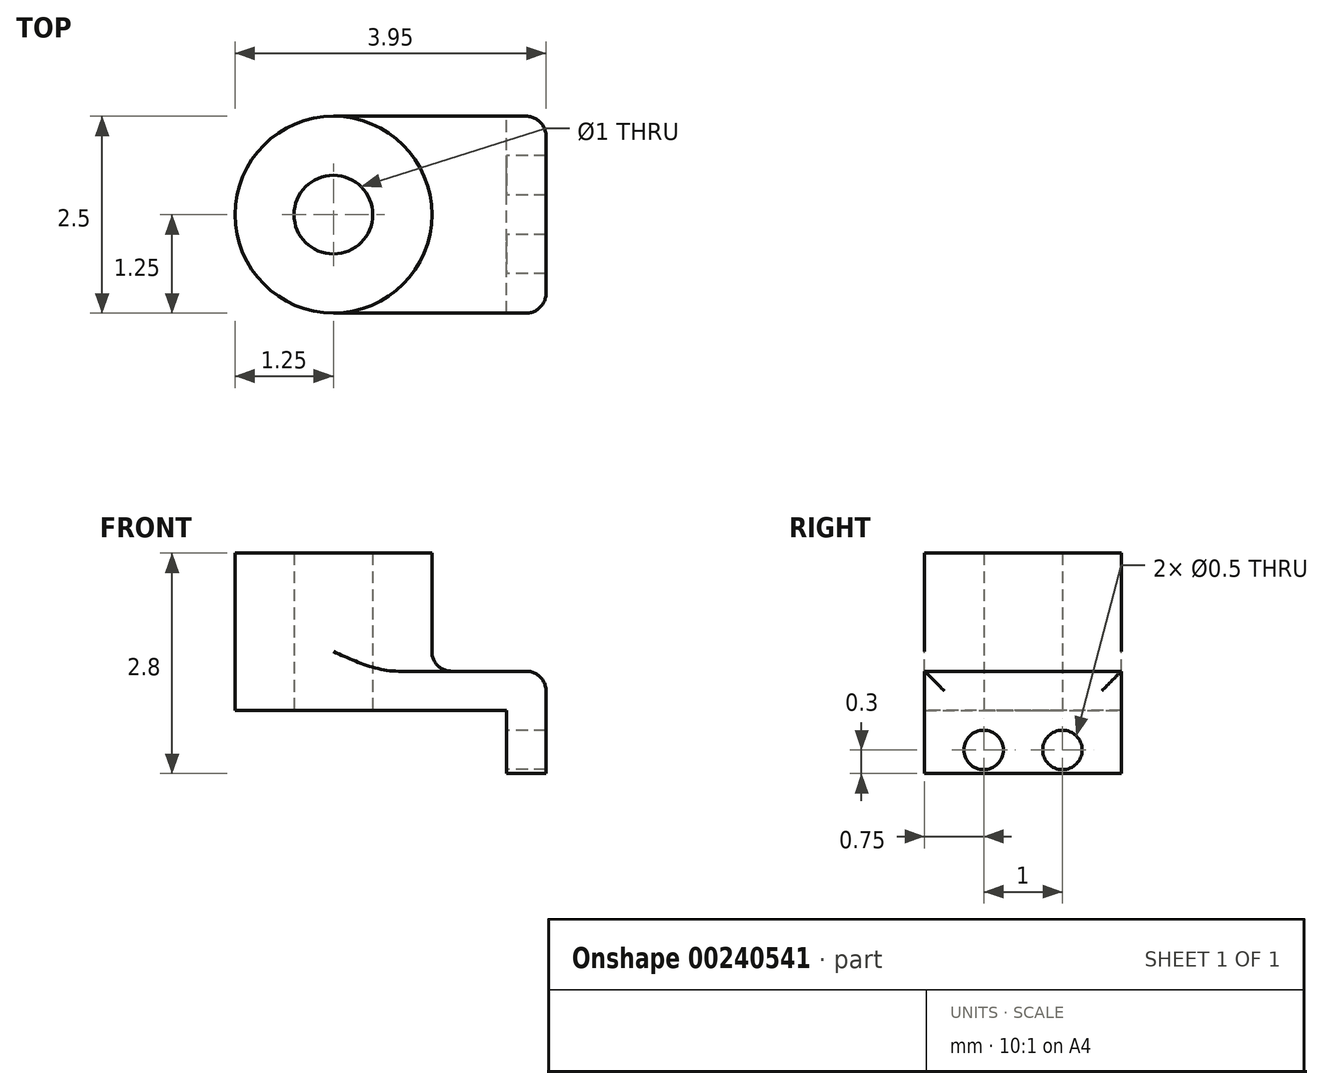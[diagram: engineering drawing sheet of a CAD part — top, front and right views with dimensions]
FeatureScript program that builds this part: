
annotation { "Feature Type Name" : "Feature", "Feature Type Description" : "" }
export const myFeature = defineFeature(function(context is Context, id is Id, definition is map)
    precondition{}
    {
        {
            var Q0;
            Q0=qCreatedBy(makeId("Top.planeOp"),FACE);
            var sketch = newSketch(context, id + "F0", { "sketchPlane" : qUnion([Q0])});
            skLineSegment(sketch, "E0.bottom", {"start": v(-1.1, -1.25) * mm, "end": v(1.1, -1.25) * mm});
            skLineSegment(sketch, "E0.top", {"start": v(-1.1, 1.25) * mm, "end": v(1.1, 1.25) * mm});
            skLineSegment(sketch, "E0.left", {"start": v(-1.1, -1.25) * mm, "end": v(-1.1, 1.25) * mm});
            skLineSegment(sketch, "E0.right", {"start": v(1.1, -1.25) * mm, "end": v(1.1, 1.25) * mm});
            skPoint(sketch, "E0.middle", {"position": v(0, 0) * mm});
            skCircle(sketch, "E1", {"center": v(-1.1, 0) * mm, "radius": 1.25 * mm});
            skCircle(sketch, "E2", {"center": v(-1.1, 0) * mm, "radius": 0.5 * mm});
            skSolve(sketch);
        }
        {
            var Q0;
            Q0 = qSketchRegion(id + "F0", true);
            extrude(context, id + "F1", {"entities" : qUnion([Q0]), "depth" : 0.5 * mm});
        }
        {
            var Q0;
            {var subQ1=sQuery(id+"F0.wireOp",EDGE,"E0.left");var subQ3=sQuery(id+"F0.wireOp",EDGE,"E2");var subQ4=makeQuery(id+"F0.imprint","INTERSECT",VERTEX,{"disambiguationData":[OD(0.0)],"derivedFrom":[subQ1,subQ3]});Q0=makeQuery(id+"F0.imprint","IMPRINT",FACE,{"disambiguationData":[TD([[makeQuery(id+"F0.imprint","IMPRINT",EDGE,{"disambiguationData":[TD([[subQ4,1.0]])],"derivedFrom":subQ3}),-1.0]])]});}
            var Q1;
            {var subQ1=sQuery(id+"F0.wireOp",EDGE,"E0.left");var subQ3=sQuery(id+"F0.wireOp",EDGE,"E2");var subQ4=makeQuery(id+"F0.imprint","INTERSECT",VERTEX,{"disambiguationData":[OD(0.0)],"derivedFrom":[subQ1,subQ3]});Q1=makeQuery(id+"F0.imprint","IMPRINT",FACE,{"disambiguationData":[TD([[makeQuery(id+"F0.imprint","IMPRINT",EDGE,{"disambiguationData":[TD([[subQ4,-1.0]])],"derivedFrom":subQ3}),-1.0]])]});}
            extrude(context, id + "F2", {"entities" : qUnion([Q0, Q1]), "operationType" : NewBodyOperationType.ADD, "depth" : 2 * mm});
        }
        {
            var Q0;
            Q0=makeQuery(id+"F1.opExtrude","SWEPT_FACE",FACE,{"disambiguationData":[OSD([sQuery(id+"F0.wireOp",EDGE,"E0.right")])]});
            var sketch = newSketch(context, id + "F3", { "sketchPlane" : qUnion([Q0])});
            skLineSegment(sketch, "E3.bottom", {"start": v(-1.25, 0.5) * mm, "end": v(1.25, 0.5) * mm});
            skLineSegment(sketch, "E3.top", {"start": v(-1.25, -0.8) * mm, "end": v(1.25, -0.8) * mm});
            skLineSegment(sketch, "E3.left", {"start": v(-1.25, 0.5) * mm, "end": v(-1.25, -0.8) * mm});
            skLineSegment(sketch, "E3.right", {"start": v(1.25, 0.5) * mm, "end": v(1.25, -0.8) * mm});
            skCircle(sketch, "E4", {"center": v(-0.5, -0.5) * mm, "radius": 0.25 * mm});
            skLineSegment(sketch, "E5", {"start": v(0, 0) * mm, "end": v(0, -0.8) * mm, "construction": true});
            skCircle(sketch, "E6.MirrorC", {"center": v(0.5, -0.5) * mm, "radius": 0.25 * mm});
            skSolve(sketch);
        }
        {
            var Q0;
            Q0 = qSketchRegion(id + "F3", true);
            extrude(context, id + "F4", {"entities" : qUnion([Q0]), "operationType" : NewBodyOperationType.ADD, "depth" : 0.5 * mm});
        }
        {
            var Q0;
            {var subQ0=sQuery(id+"F0.wireOp",EDGE,"E1");Q0=makeQuery(id+"F2.boolean.opBoolean","INTERSECT",EDGE,{"derivedFrom":[makeQuery(id+"F1.opExtrude","CAP_FACE",FACE,{"disambiguationData":[OSD([sQuery(id+"F0.wireOp",EDGE,"E0.bottom"),sQuery(id+"F0.wireOp",EDGE,"E0.top"),sQuery(id+"F0.wireOp",EDGE,"E0.right"),subQ0,sQuery(id+"F0.wireOp",EDGE,"E2")])],"isStart":false}),makeQuery(id+"F2.opExtrude","SWEPT_FACE",FACE,{"disambiguationData":[OSD([subQ0])]})]});}
            var Q1;
            Q1=makeQuery(id+"F4.opExtrude","CAP_EDGE",EDGE,{"disambiguationData":[OSD([sQuery(id+"F3.wireOp",EDGE,"E3.bottom")])],"isStart":false});
            var Q2;
            Q2=makeQuery(id+"F4.opExtrude","CAP_EDGE",EDGE,{"disambiguationData":[OSD([sQuery(id+"F3.wireOp",EDGE,"E3.left")])],"isStart":false});
            var Q3;
            Q3=makeQuery(id+"F4.opExtrude","CAP_EDGE",EDGE,{"disambiguationData":[OSD([sQuery(id+"F3.wireOp",EDGE,"E3.right")])],"isStart":false});
            fillet(context, id + "F5", {"entities" : qUnion([Q0, Q1, Q2, Q3]), "radius" : .25 * mm, "tangentPropagation" : true, "allowEdgeOverflow" : false});
        }
    });
